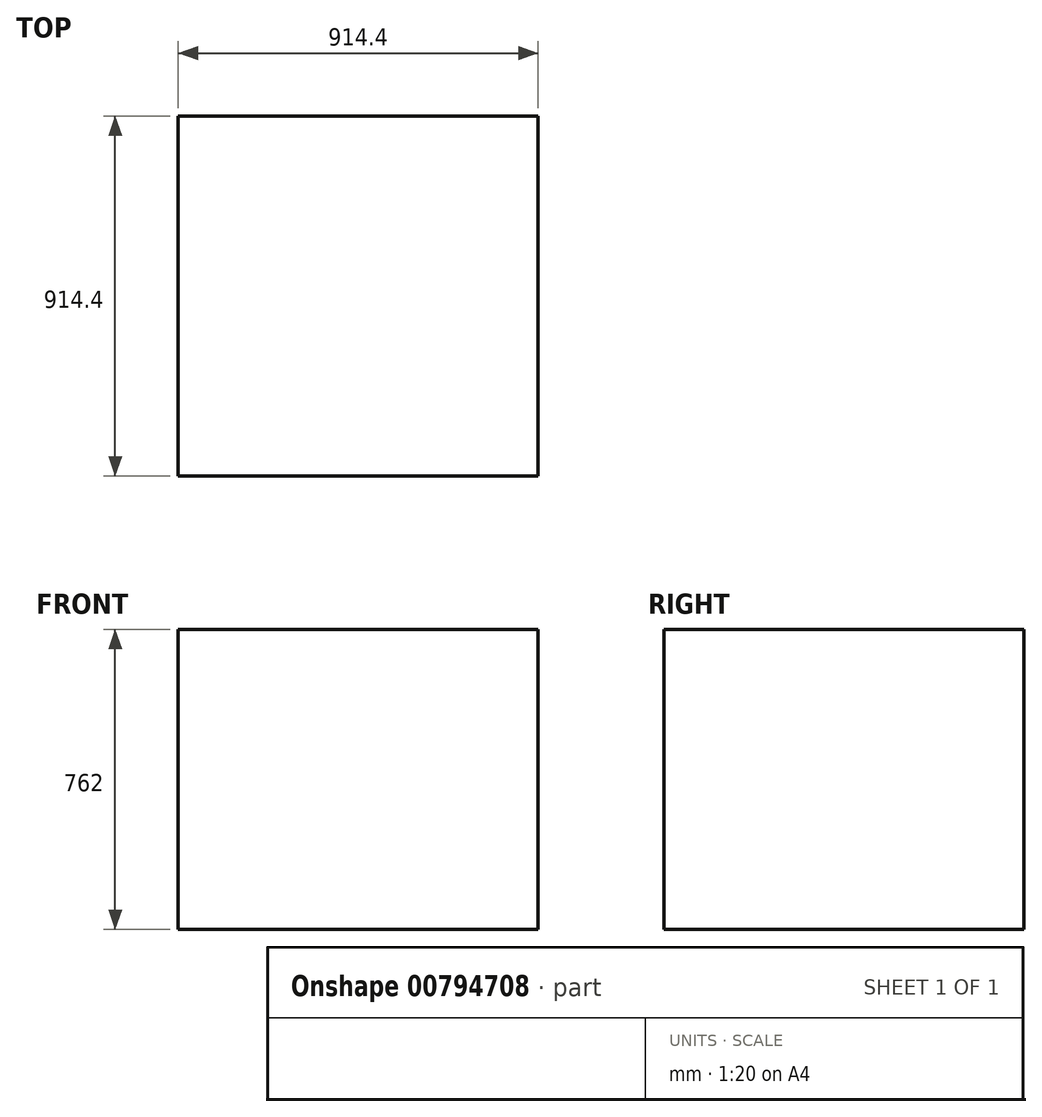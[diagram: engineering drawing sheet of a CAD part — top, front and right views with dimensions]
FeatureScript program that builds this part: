
annotation { "Feature Type Name" : "Feature", "Feature Type Description" : "" }
export const myFeature = defineFeature(function(context is Context, id is Id, definition is map)
    precondition{}
    {
        {
            var Q0;
            Q0=qCreatedBy(makeId("Top.planeOp"),FACE);
            var sketch = newSketch(context, id + "F0", { "sketchPlane" : qUnion([Q0])});
            skLineSegment(sketch, "E0.rect.bottom", {"start": v(457.2, -457.2) * mm, "end": v(-457.2, -457.2) * mm});
            skLineSegment(sketch, "E0.rect.top", {"start": v(457.2, 457.2) * mm, "end": v(-457.2, 457.2) * mm});
            skLineSegment(sketch, "E0.rect.left", {"start": v(457.2, -457.2) * mm, "end": v(457.2, 457.2) * mm});
            skLineSegment(sketch, "E0.rect.right", {"start": v(-457.2, -457.2) * mm, "end": v(-457.2, 457.2) * mm});
            skPoint(sketch, "E0.rect.middle", {"position": v(0, 0) * mm});
            skSolve(sketch);
        }
        {
            var Q0;
            Q0=makeQuery(id+"F0.imprint","IMPRINT",FACE,{"disambiguationData":[TD([[makeQuery(id+"F0.imprint","IMPRINT",EDGE,{"derivedFrom":sQuery(id+"F0.wireOp",EDGE,"E0.rect.bottom")}),-1.0]])]});
            extrude(context, id + "F1", {"entities" : qUnion([Q0]), "depth" : 762 * mm});
        }
    });
